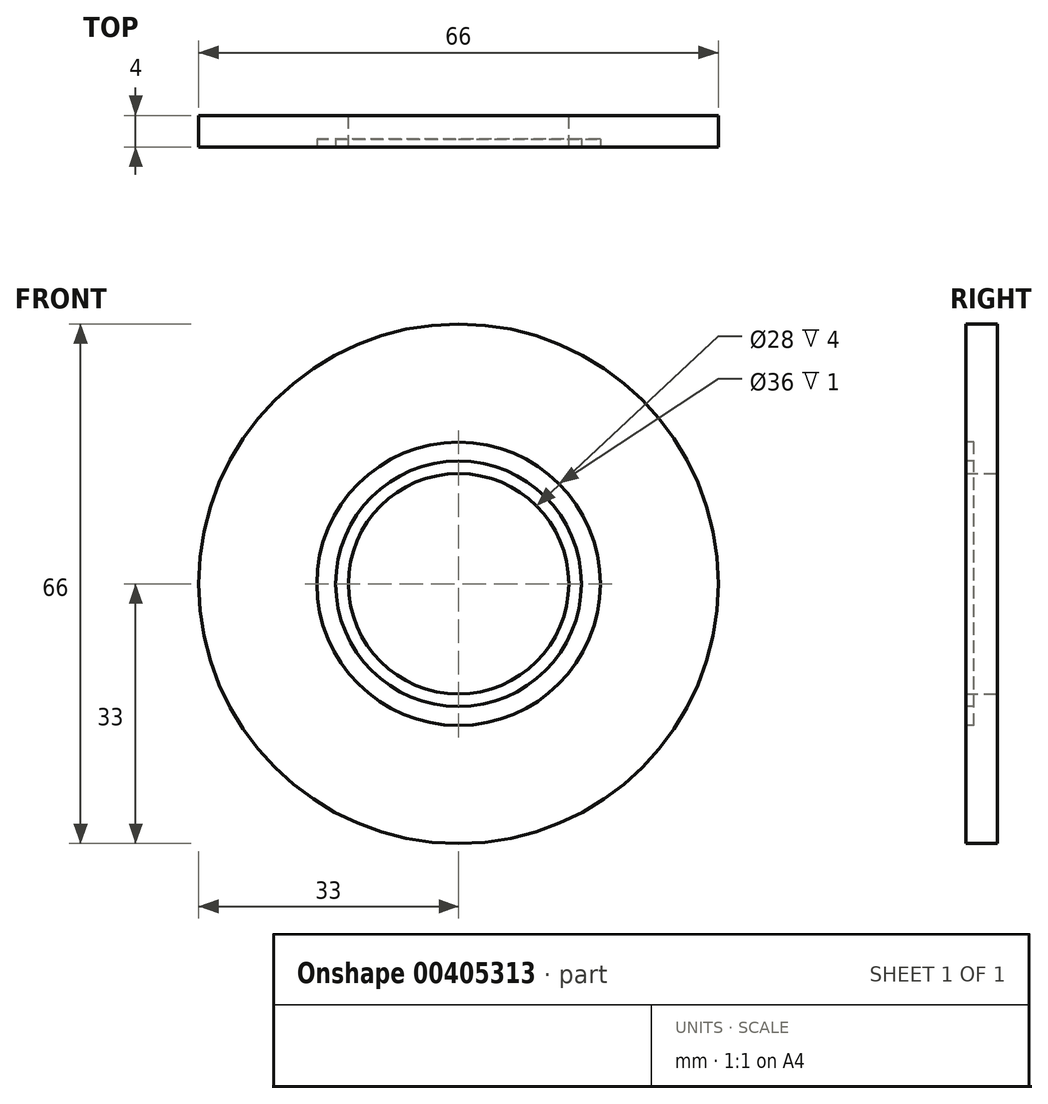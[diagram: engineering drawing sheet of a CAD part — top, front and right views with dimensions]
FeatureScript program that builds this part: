
annotation { "Feature Type Name" : "Feature", "Feature Type Description" : "" }
export const myFeature = defineFeature(function(context is Context, id is Id, definition is map)
    precondition{}
    {
        {
            var Q0;
            Q0=qCreatedBy(makeId("Front.planeOp"),FACE);
            var sketch = newSketch(context, id + "F0", { "sketchPlane" : qUnion([Q0])});
            skCircle(sketch, "E0", {"center": v(0, 0) * mm, "radius": 14 * mm});
            skCircle(sketch, "E1", {"center": v(0, 0) * mm, "radius": 33 * mm});
            skSolve(sketch);
        }
        {
            var Q0;
            Q0=makeQuery(id+"F0.imprint","IMPRINT",FACE,{"disambiguationData":[TD([[makeQuery(id+"F0.imprint","IMPRINT",EDGE,{"derivedFrom":sQuery(id+"F0.wireOp",EDGE,"E0")}),-1.0]])]});
            extrude(context, id + "F1", {"entities" : qUnion([Q0]), "depth" : 4 * mm});
        }
        {
            var Q0;
            Q0=makeQuery(id+"F1.opExtrude","CAP_FACE",FACE,{"disambiguationData":[OSD([sQuery(id+"F0.wireOp",EDGE,"E0"),sQuery(id+"F0.wireOp",EDGE,"E1")])],"isStart":false});
            var sketch = newSketch(context, id + "F2", { "sketchPlane" : qUnion([Q0])});
            skCircle(sketch, "E2", {"center": v(0, 0) * mm, "radius": 18 * mm});
            skCircle(sketch, "E3", {"center": v(0, 0) * mm, "radius": 15.6 * mm});
            skLineSegment(sketch, "E4", {"start": v(0, 15.6) * mm, "end": v(0, 18) * mm});
            skSolve(sketch);
        }
        {
            var Q0;
            Q0 = qSketchRegion(id + "F2", true);
            extrude(context, id + "F3", {"entities" : qUnion([Q0]), "operationType" : NewBodyOperationType.REMOVE, "oppositeDirection" : true, "depth" : 1 * mm});
        }
    });
